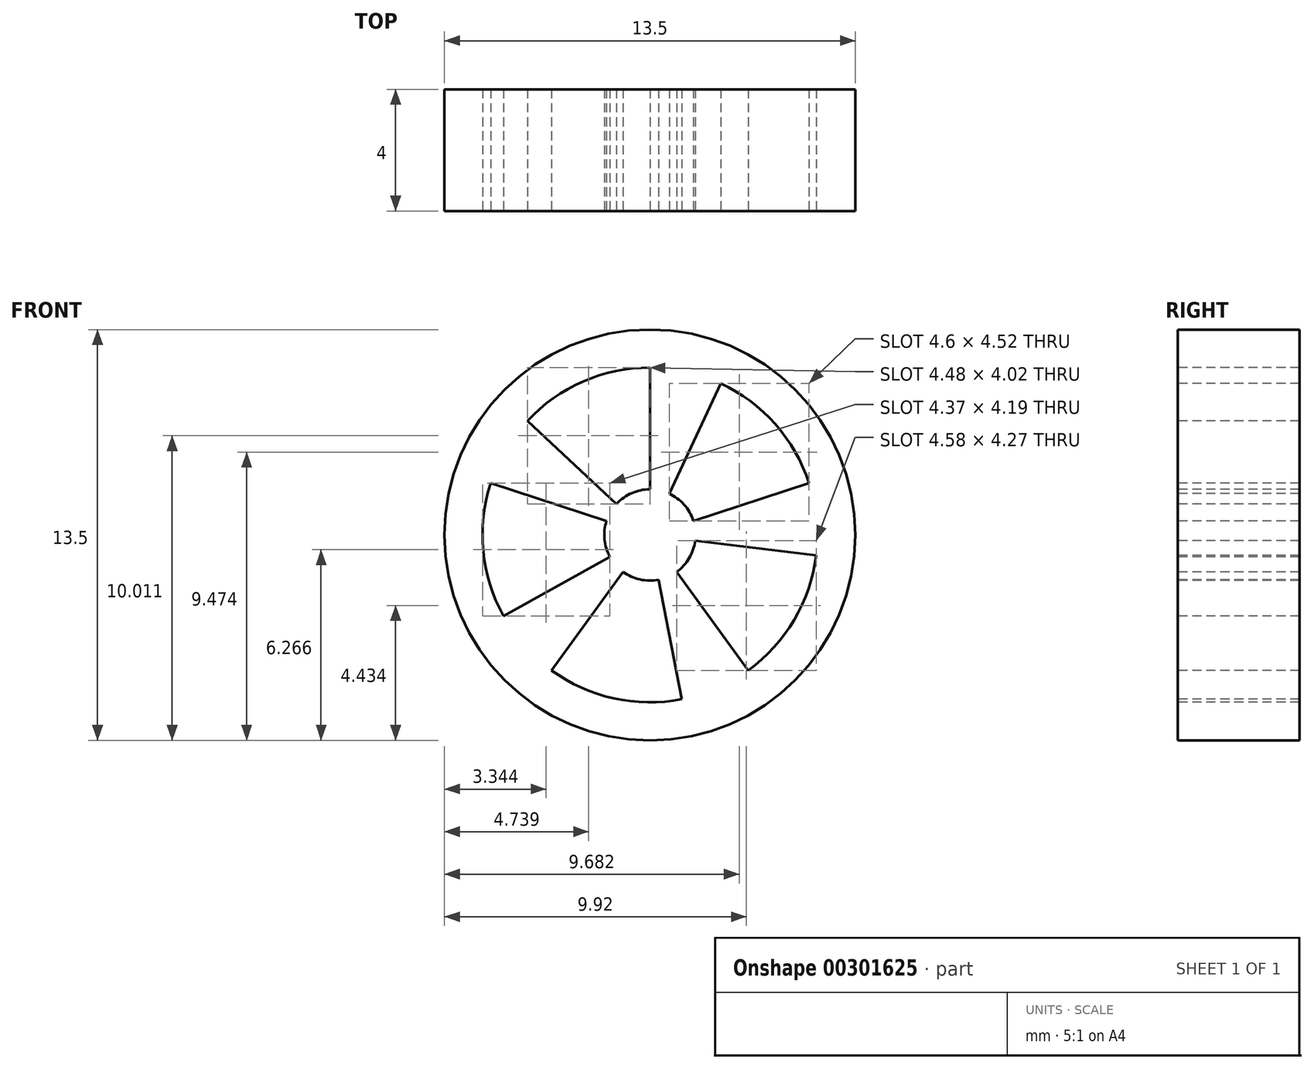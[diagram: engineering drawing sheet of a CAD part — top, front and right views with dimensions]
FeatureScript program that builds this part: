
annotation { "Feature Type Name" : "Feature", "Feature Type Description" : "" }
export const myFeature = defineFeature(function(context is Context, id is Id, definition is map)
    precondition{}
    {
        {
            var Q0;
            Q0=qCreatedBy(makeId("Front.planeOp"),FACE);
            var sketch = newSketch(context, id + "F0", { "sketchPlane" : qUnion([Q0])});
            skCircle(sketch, "E0", {"center": v(0, 0) * mm, "radius": 6.75 * mm});
            skSolve(sketch);
        }
        {
            var Q0;
            Q0 = qSketchRegion(id + "F0", true);
            extrude(context, id + "F1", {"entities" : qUnion([Q0]), "depth" : 4 * mm});
        }
        {
            var Q0;
            Q0=makeQuery(id+"F1.opExtrude","CAP_FACE",FACE,{"disambiguationData":[OSD([sQuery(id+"F0.wireOp",EDGE,"E0")])],"isStart":false});
            var sketch = newSketch(context, id + "F2", { "sketchPlane" : qUnion([Q0])});
            skCircle(sketch, "E1", {"center": v(0, 0) * mm, "radius": 5.5 * mm});
            skCircle(sketch, "E2", {"center": v(0, 0) * mm, "radius": 1.5 * mm});
            skLineSegment(sketch, "E3", {"start": v(0, 5.5) * mm, "end": v(0, 1.5) * mm});
            skLineSegment(sketch, "E4", {"start": v(2.32, 4.98) * mm, "end": v(0.63, 1.36) * mm});
            skLineSegment(sketch, "E5.1.0", {"start": v(-5.23, 1.7) * mm, "end": v(-1.43, 0.46) * mm});
            skLineSegment(sketch, "E5.1.1", {"start": v(-4.02, 3.75) * mm, "end": v(-1.1, 1.02) * mm});
            skLineSegment(sketch, "E5.2.0", {"start": v(-3.23, -4.45) * mm, "end": v(-0.88, -1.21) * mm});
            skLineSegment(sketch, "E5.2.1", {"start": v(-4.81, -2.67) * mm, "end": v(-1.31, -0.73) * mm});
            skLineSegment(sketch, "E5.3.0", {"start": v(3.23, -4.45) * mm, "end": v(0.88, -1.21) * mm});
            skLineSegment(sketch, "E5.3.1", {"start": v(1.05, -5.4) * mm, "end": v(0.29, -1.47) * mm});
            skLineSegment(sketch, "E5.4.0", {"start": v(5.23, 1.7) * mm, "end": v(1.43, 0.46) * mm});
            skLineSegment(sketch, "E5.4.1", {"start": v(5.46, -0.67) * mm, "end": v(1.49, -0.18) * mm});
            skSolve(sketch);
        }
        {
            var Q0;
            {var subQ0=sQuery(id+"F2.wireOp",EDGE,"E3");Q0=makeQuery(id+"F2.imprint","IMPRINT",FACE,{"disambiguationData":[TD([[makeQuery(id+"F2.imprint","IMPRINT",EDGE,{"derivedFrom":subQ0}),-1.0]])]});}
            var Q1;
            {var subQ0=sQuery(id+"F2.wireOp",EDGE,"E4");Q1=makeQuery(id+"F2.imprint","IMPRINT",FACE,{"disambiguationData":[TD([[makeQuery(id+"F2.imprint","IMPRINT",EDGE,{"derivedFrom":subQ0}),1.0]])]});}
            var Q2;
            {var subQ0=sQuery(id+"F2.wireOp",EDGE,"E5.3.0");Q2=makeQuery(id+"F2.imprint","IMPRINT",FACE,{"disambiguationData":[TD([[makeQuery(id+"F2.imprint","IMPRINT",EDGE,{"derivedFrom":subQ0}),-1.0]])]});}
            var Q3;
            {var subQ0=sQuery(id+"F2.wireOp",EDGE,"E5.2.0");Q3=makeQuery(id+"F2.imprint","IMPRINT",FACE,{"disambiguationData":[TD([[makeQuery(id+"F2.imprint","IMPRINT",EDGE,{"derivedFrom":subQ0}),-1.0]])]});}
            var Q4;
            {var subQ0=sQuery(id+"F2.wireOp",EDGE,"E5.1.0");Q4=makeQuery(id+"F2.imprint","IMPRINT",FACE,{"disambiguationData":[TD([[makeQuery(id+"F2.imprint","IMPRINT",EDGE,{"derivedFrom":subQ0}),-1.0]])]});}
            extrude(context, id + "F3", {"entities" : qUnion([Q0, Q1, Q2, Q3, Q4]), "operationType" : NewBodyOperationType.REMOVE, "oppositeDirection" : true, "depth" : 25 * mm});
        }
    });
